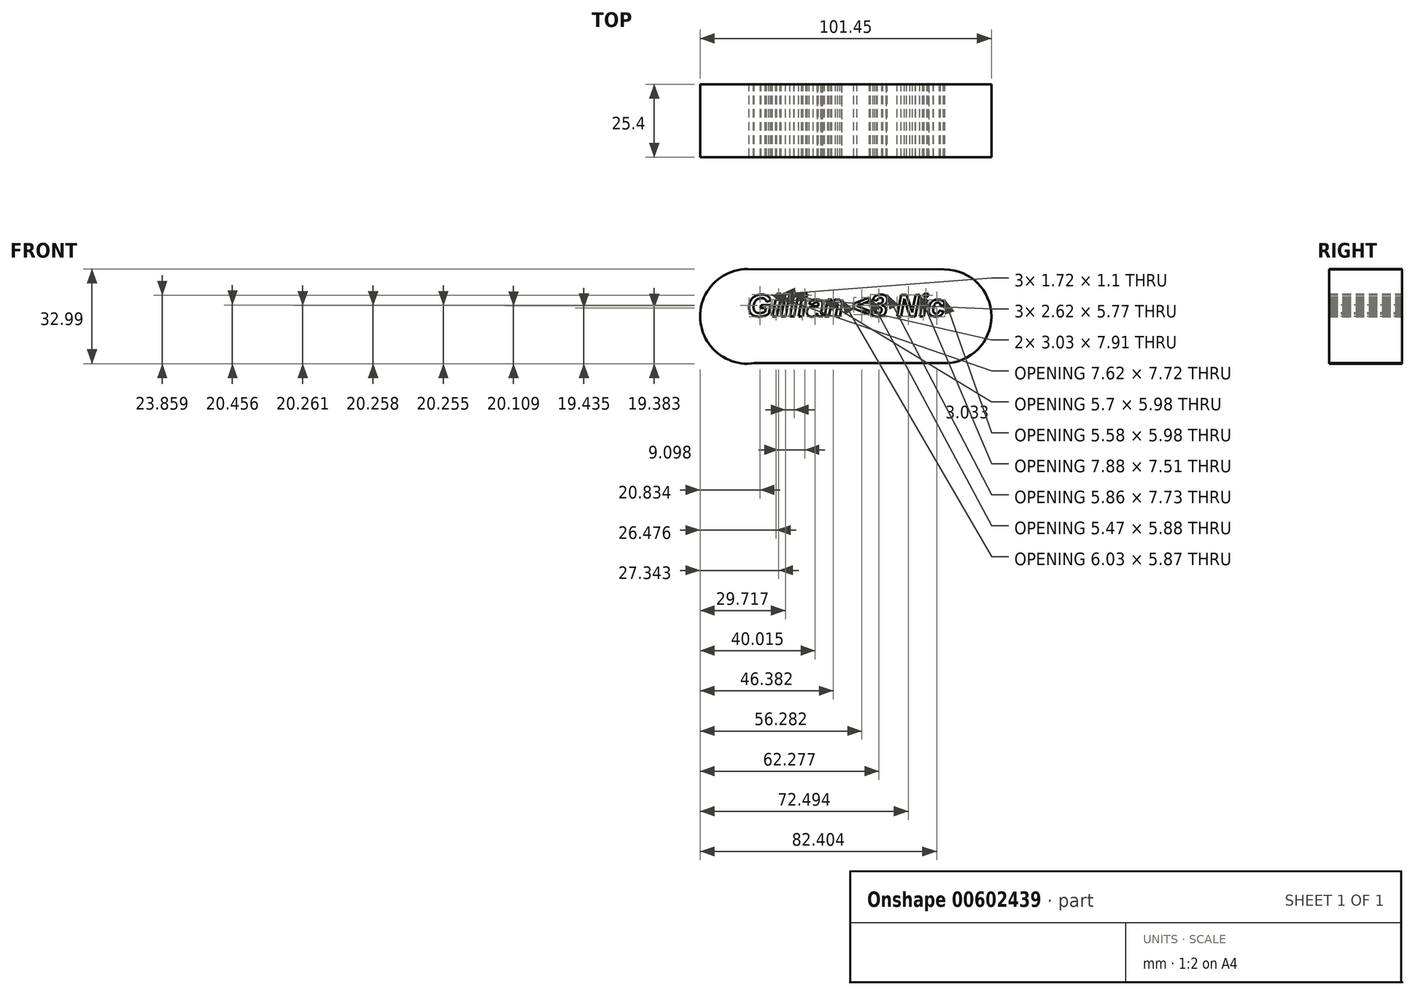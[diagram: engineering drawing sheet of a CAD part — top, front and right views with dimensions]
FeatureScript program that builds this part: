
annotation { "Feature Type Name" : "Feature", "Feature Type Description" : "" }
export const myFeature = defineFeature(function(context is Context, id is Id, definition is map)
    precondition{}
    {
        {
            var Q0;
            Q0=qCreatedBy(makeId("Front.planeOp"),FACE);
            var sketch = newSketch(context, id + "F0", { "sketchPlane" : qUnion([Q0])});
            skArc(sketch, "E0", {"start": v(-39.71, 37.07) * mm, "mid": v(-56.2, 19.4) * mm, "end": v(-37.37, 4.25) * mm});
            skLineSegment(sketch, "E1", {"start": v(-39.71, 37.07) * mm, "end": v(28.87, 36.93) * mm});
            skLineSegment(sketch, "E2", {"start": v(-37.37, 4.25) * mm, "end": v(28.87, 4.25) * mm});
            skArc(sketch, "E3", {"start": v(28.87, 4.25) * mm, "mid": v(45.21, 20.6) * mm, "end": v(28.87, 36.93) * mm});
            skText(sketch, "E4", { "text": "Gillian <3 Nic", "fontName": "Arimo-BoldItalic.ttf"});
            const initialGuessF0  = {"E4": [-0.03975, 0.02058, 1, 0, 0.00786]};
            skSetInitialGuess(sketch, initialGuessF0);
            skSolve(sketch);
        }
        {
            var Q0;
            Q0 = qSketchRegion(id + "F0", true);
            extrude(context, id + "F1", {"entities" : qUnion([Q0]), "depth" : 25.4 * mm, "offsetDistance" : 25.4 * mm});
        }
    });
